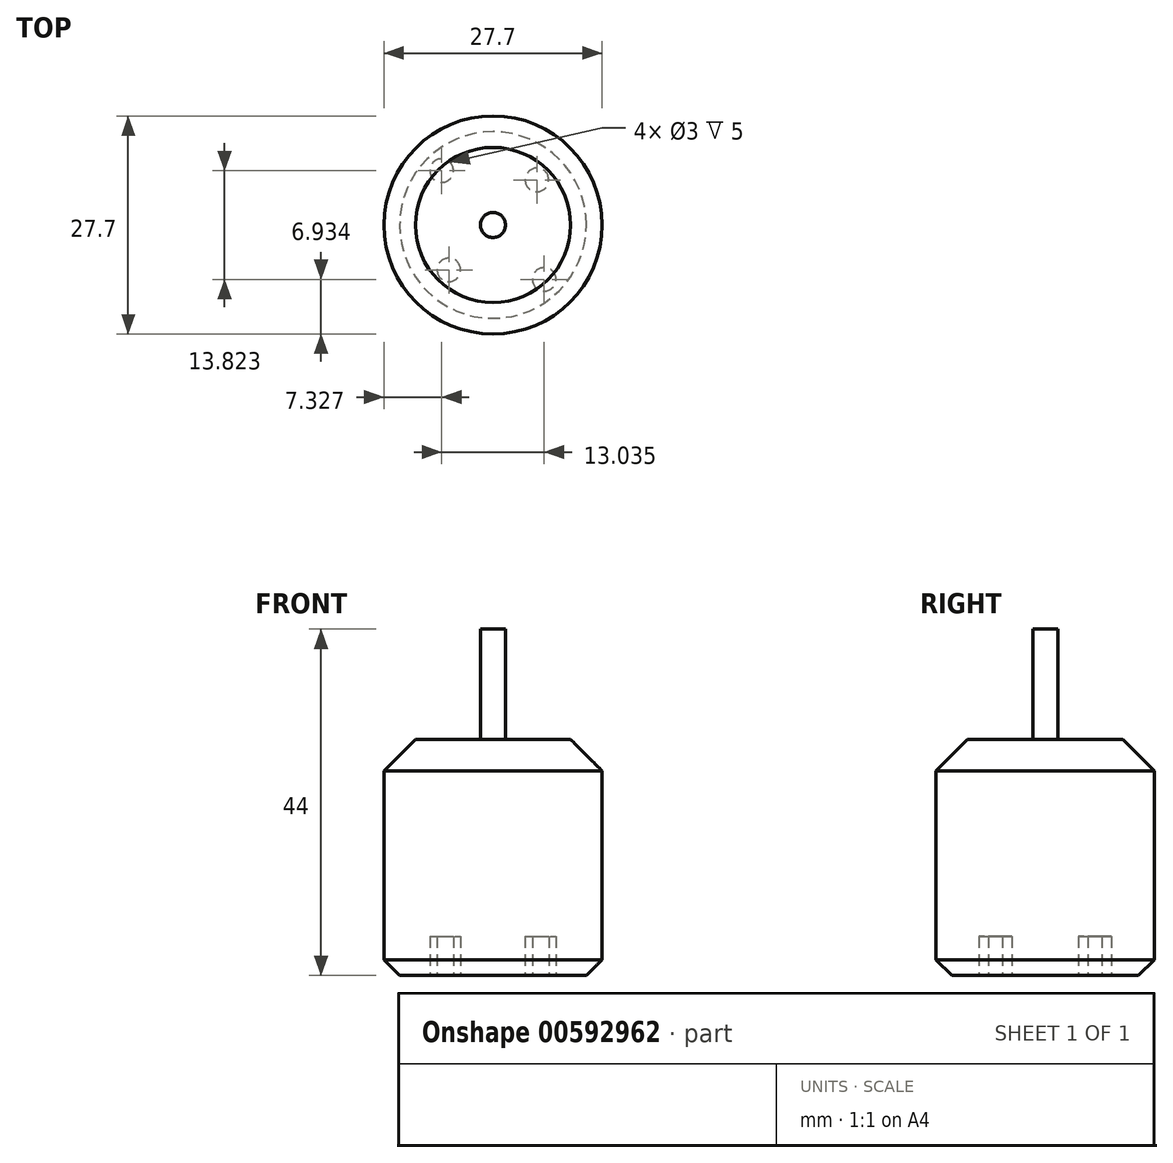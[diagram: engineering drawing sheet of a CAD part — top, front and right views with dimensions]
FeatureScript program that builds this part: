
annotation { "Feature Type Name" : "Feature", "Feature Type Description" : "" }
export const myFeature = defineFeature(function(context is Context, id is Id, definition is map)
    precondition{}
    {
        {
            var Q0;
            Q0=qCreatedBy(makeId("Top.planeOp"),FACE);
            var sketch = newSketch(context, id + "F0", { "sketchPlane" : qUnion([Q0])});
            skCircle(sketch, "E0", {"center": v(0, 0) * mm, "radius": 13.85 * mm});
            skSolve(sketch);
        }
        {
            var Q0;
            Q0=makeQuery(id+"F0.imprint","IMPRINT",FACE,{"disambiguationData":[TD([[makeQuery(id+"F0.imprint","IMPRINT",EDGE,{"derivedFrom":sQuery(id+"F0.wireOp",EDGE,"E0")}),1.0]])]});
            extrude(context, id + "F1", {"entities" : qUnion([Q0]), "depth" : 30 * mm, "offsetDistance" : 25 * mm});
        }
        {
            var Q0;
            Q0=makeQuery(id+"F1.opExtrude","CAP_EDGE",EDGE,{"disambiguationData":[OSD([sQuery(id+"F0.wireOp",EDGE,"E0")])],"isStart":false});
            chamfer(context, id + "F2", {"entities" : qUnion([Q0]), "width" : 4 * mm, "tangentPropagation" : true});
        }
        {
            var Q0;
            Q0=makeQuery(id+"F1.opExtrude","CAP_FACE",FACE,{"disambiguationData":[OSD([sQuery(id+"F0.wireOp",EDGE,"E0")])],"isStart":false});
            var sketch = newSketch(context, id + "F3", { "sketchPlane" : qUnion([Q0])});
            skCircle(sketch, "E1", {"center": v(0, 0) * mm, "radius": 1.59 * mm});
            skSolve(sketch);
        }
        {
            var Q0;
            Q0=makeQuery(id+"F3.imprint","IMPRINT",FACE,{"disambiguationData":[TD([[makeQuery(id+"F3.imprint","IMPRINT",EDGE,{"derivedFrom":sQuery(id+"F3.wireOp",EDGE,"E1")}),1.0]])]});
            extrude(context, id + "F4", {"entities" : qUnion([Q0]), "operationType" : NewBodyOperationType.ADD, "depth" : 14 * mm, "offsetDistance" : 25 * mm});
        }
        {
            var Q0;
            Q0=makeQuery(id+"F1.opExtrude","CAP_EDGE",EDGE,{"disambiguationData":[OSD([sQuery(id+"F0.wireOp",EDGE,"E0")])],"isStart":true});
            chamfer(context, id + "F5", {"entities" : qUnion([Q0]), "width" : 2 * mm, "tangentPropagation" : true});
        }
        {
            var Q0;
            Q0=makeQuery(id+"F1.opExtrude","CAP_FACE",FACE,{"disambiguationData":[OSD([sQuery(id+"F0.wireOp",EDGE,"E0")])],"isStart":true});
            var sketch = newSketch(context, id + "F6", { "sketchPlane" : qUnion([Q0])});
            skLineSegment(sketch, "E2", {"start": v(-6.52, -6.9) * mm, "end": v(6.51, 6.92) * mm, "construction": true});
            skLineSegment(sketch, "E3", {"start": v(5.59, -5.72) * mm, "end": v(-5.6, 5.71) * mm, "construction": true});
            skCircle(sketch, "E4", {"center": v(6.51, 6.92) * mm, "radius": 1.5 * mm});
            skCircle(sketch, "E5", {"center": v(-5.6, 5.71) * mm, "radius": 1.5 * mm});
            skCircle(sketch, "E6", {"center": v(-6.52, -6.9) * mm, "radius": 1.5 * mm});
            skCircle(sketch, "E7", {"center": v(5.59, -5.72) * mm, "radius": 1.5 * mm});
            skSolve(sketch);
        }
        {
            var Q0;
            Q0=makeQuery(id+"F6.imprint","IMPRINT",FACE,{"disambiguationData":[TD([[makeQuery(id+"F6.imprint","IMPRINT",EDGE,{"derivedFrom":sQuery(id+"F6.wireOp",EDGE,"E7")}),1.0]])]});
            var Q1;
            Q1=makeQuery(id+"F6.imprint","IMPRINT",FACE,{"disambiguationData":[TD([[makeQuery(id+"F6.imprint","IMPRINT",EDGE,{"derivedFrom":sQuery(id+"F6.wireOp",EDGE,"E4")}),1.0]])]});
            var Q2;
            Q2=makeQuery(id+"F6.imprint","IMPRINT",FACE,{"disambiguationData":[TD([[makeQuery(id+"F6.imprint","IMPRINT",EDGE,{"derivedFrom":sQuery(id+"F6.wireOp",EDGE,"E5")}),1.0]])]});
            var Q3;
            Q3=makeQuery(id+"F6.imprint","IMPRINT",FACE,{"disambiguationData":[TD([[makeQuery(id+"F6.imprint","IMPRINT",EDGE,{"derivedFrom":sQuery(id+"F6.wireOp",EDGE,"E6")}),1.0]])]});
            extrude(context, id + "F7", {"entities" : qUnion([Q0, Q1, Q2, Q3]), "operationType" : NewBodyOperationType.REMOVE, "oppositeDirection" : true, "depth" : 5 * mm, "offsetDistance" : 25 * mm});
        }
    });
